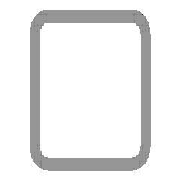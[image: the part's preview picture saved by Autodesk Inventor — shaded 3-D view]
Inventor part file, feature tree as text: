
AUTODESK INVENTOR PART (.ipt)
format: ipt  version: 2024 (Build 280153000, 153)  size: 140,800 bytes
history: native  units: mm (DEFAULTED — no unit token found)
features: other x4, sketch x1, plane x1
ambient origin geometry x8: Origin, YZ Plane, XZ Plane, XY Plane, X Axis, Y Axis, Z Axis, Center Point
bodies: Solid1 (feature_tree), Body (feature_tree)
feature tree (6):
  parser-record x1  (decoder bookkeeping rows leaked as tree rows — omitted from the tree; the rows remain in map.json)
  other  "Driven Length"
  other  "Start Plane"
  other  "End Plane"
  sketch  "Sketch3"  dims[d3=748.0mm d4=0.0mm d7=7.5mm d10=100.0mm d11=100.0mm d12=5.0mm d13=-0.0mm d14=748.0mm d15=50.0mm d16=50.0mm d17=90.0deg d18=748.0mm d19=5.0mm d20=5.0mm]
  plane  "Work Plane3"
